# Revit family: NBS_Senator_OffcTbls_Ad-libTablesUK_SoftSquare-SingleLeg
name_source: partatom
category: Furniture
revit_build: Autodesk Revit 2016 (Build: 20151007_0715(x64)
units: mm (PartAtom-declared; Revit-internal decimal feet)

## family parameters
Always vertical = Yes
Cut with Voids When Loaded = No
Room Calculation Point = No
Shared = No
Work Plane-Based = No

## types (3) — shared parameters
AssetType = Moveable
CablePortCoverMaterial = NBS_Concept
Category = Pr_40_50_21_60:Office tables
CodePerformance = BS EN 15372 2008, BS 6396 2008
ColourOptions = Carini walnut, mocha, autumn, strata oak, maple, highland oak, beech, winter oak, hacienda white, white, light grey, denim, clay, bordeaux, lemon sorbet, Formica  fundamentals, polyrey, durion
ColumnMaterial = NBS_Concept
Description = Soft square table with 4 star base
DimensionsPlanSize = 800 x 800 mm
DurationUnit = year
ExpectedLife = 15
ExposedEdgesOptions = Ply effect edging, silver ply edging
Finish = MFC
FinishOptions = MFC, MFMDF, laminate
FootHeight = 10 mm  [stored 0.0328084 ft]
FrameMountingMaterial = NBS_Concept
FramesColourOptions = Black, slate grey, light grey
FramesSupports = 4 Star base tables utilise an aluminium base and top casting with a steel column
HasProfileEdge = No
IfcExportAs = IfcFurnitureType
IfcExportType = TABLE
IsBuiltIn = No
MainColor = User to populate
ManufacturerName = Senator
ManufacturerURL = www.senator.co.uk
ModelReference = Ad-lib tables soft square UK
NBSCertification = www.nationalbimlibrary.com/cert/frwd40rv
NBSDescription = Office tables
NBSReference = 45-35-20/340
NominalDepth = 800 mm  [stored 2.62467 ft]
NominalLength = 800 mm  [stored 2.62467 ft]
PostHeight = 550 mm
PostMaterial = NBS_Concept
ProductInformation = www.Senator.com/FamilyDocuments/474/Senator_SPEC_2017_%20ADLIB%20Tables_v9%20WEB.pdf
Status = UNSET
SustainabilityPerformance = 99% recycleable
TableTopLength = 800 mm  [stored 2.62467 ft]
TableTopWidth = 800 mm  [stored 2.62467 ft]
Uniclass2015Code = Pr_40_50_21_60
Uniclass2015Title = Office tables
Uniclass2015Version = Products v1.9
Version = 1
WarrantyDescription = Senator warrants that its manufactured products are free from defects for a period of fifteen years on Senator desking ranges
WarrantyDurationParts = 15
WarrantyDurationUnit = year
WorksurfaceArea = 0.64 m²
WorktopLaminate = No
WorktopMFC = Yes
WorktopMFMDF = No
WorktopMaterial = NBS_Concept
WorktopMaterialTapedEdge = NBS_Concept
WorktopThickness = 25 mm  [stored 0.082021 ft]
WorktopType = NBS_Senator_OffcTbls_Ad-libTablesUK_SoftSquareMFC : SoftSquareMFC
WorktopTypeLaminate = NBS_Senator_OffcTbls_Ad-libTablesUK_SoftSquareLaminate : SoftSquareLaminate
WorktopTypeMFC = NBS_Senator_OffcTbls_Ad-libTablesUK_SoftSquareMFC : SoftSquareMFC
WorktopTypeMFMDF = NBS_Senator_OffcTbls_Ad-libTablesUK_SoftSquareMFMDF : SoftSquareMFMDF
zero-valued in all types: NominalWidth, NumberOfChairs

## per-type parameters (varying)
| type | BIMObjectName | Name | NominalHeight | Size | WorktopHeight |
| ALP08SS | NBS_Senator_OfficeTables_Ad-libTablesUK_SoftSquare_ALP08SS | OfficeTables_Ad-libTablesUK_SoftSquare_ALP08SS_Senator | 740 mm | 800 x 800 x 740 mm | 740 mm |
| ALP08SSC | NBS_Senator_OfficeTables_Ad-libTablesUK_SoftSquare_ALP08SSC | OfficeTables_Ad-libTablesUK_SoftSquare_ALP08SSC_Senator | 400 mm  [stored 1.31234 ft] | 800 x 800 x 400 mm | 400 mm  [stored 1.31234 ft] |
| ALP08SSP | NBS_Senator_OfficeTables_Ad-libTablesUK_SoftSquare_ALP08SSP | OfficeTables_Ad-libTablesUK_SoftSquare_ALP08SSP_Senator | 1050 mm | 800 x 800 x 1050 mm | 1050 mm |

note: column(s) folded — value = type name in every type: ModelNumber

note: [stored X ft] marks values corroborated as IEEE doubles in the binary element streams (Revit-internal decimal feet)

## geometry (parser evidence)
native form markers: Sweep x14
no freeform markers — native parametric forms only
